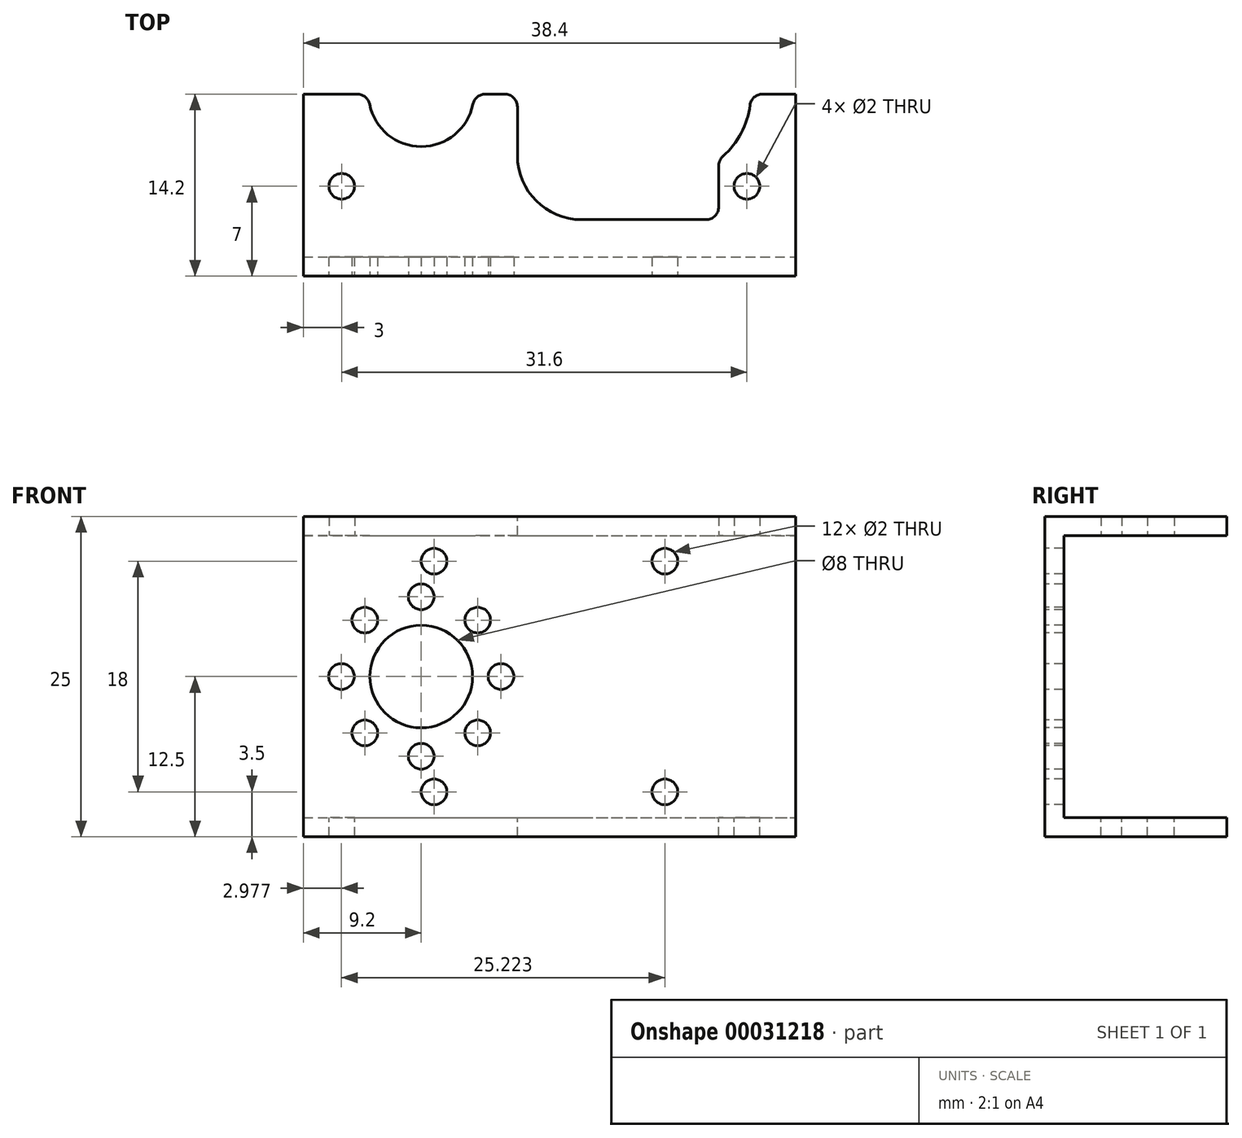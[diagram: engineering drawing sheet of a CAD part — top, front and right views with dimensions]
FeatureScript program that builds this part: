
annotation { "Feature Type Name" : "Feature", "Feature Type Description" : "" }
export const myFeature = defineFeature(function(context is Context, id is Id, definition is map)
    precondition{}
    {
        {
            var Q0;
            Q0=qCreatedBy(makeId("Top.planeOp"),FACE);
            var sketch = newSketch(context, id + "F0", { "sketchPlane" : qUnion([Q0])});
            skLineSegment(sketch, "E0.bottom", {"start": v(19.2, -14.2) * mm, "end": v(-19.2, -14.2) * mm});
            skLineSegment(sketch, "E0.top", {"start": v(19.2, 14.2) * mm, "end": v(-19.2, 14.2) * mm});
            skLineSegment(sketch, "E0.left", {"start": v(19.2, -14.2) * mm, "end": v(19.2, 14.2) * mm});
            skLineSegment(sketch, "E0.right", {"start": v(-19.2, -14.2) * mm, "end": v(-19.2, 14.2) * mm});
            skPoint(sketch, "E0.middle", {"position": v(0, 0) * mm});
            skCircle(sketch, "E1", {"center": v(-10, 0) * mm, "radius": 4.1 * mm});
            skCircle(sketch, "E2", {"center": v(-16.2, 7.2) * mm, "radius": 1 * mm});
            skCircle(sketch, "E3", {"center": v(15.4, 7.2) * mm, "radius": 1 * mm});
            skLineSegment(sketch, "E4.bottom", {"start": v(2.5, 9.8) * mm, "end": v(12.2, 9.8) * mm});
            skLineSegment(sketch, "E4.top", {"start": v(2.5, -9.8) * mm, "end": v(12.2, -9.8) * mm});
            skLineSegment(sketch, "E4.left", {"start": v(-2.5, 4.8) * mm, "end": v(-2.5, -4.8) * mm});
            skLineSegment(sketch, "E4.right", {"start": v(13.2, 8.8) * mm, "end": v(13.2, 5.6) * mm});
            skPoint(sketch, "E4.middle", {"position": v(5.35, 0) * mm});
            skPoint(sketch, "E5.visualSharp", {"position": v(-2.5, 9.8) * mm});
            skArc(sketch, "E5.filletArc", {"start": v(2.5, 9.8) * mm, "mid": v(-1.04, 8.34) * mm, "end": v(-2.5, 4.8) * mm});
            skPoint(sketch, "E6.visualSharp", {"position": v(-2.5, -9.8) * mm});
            skArc(sketch, "E6.filletArc", {"start": v(-2.5, -4.8) * mm, "mid": v(-1.04, -8.34) * mm, "end": v(2.5, -9.8) * mm});
            skPoint(sketch, "E7.visualSharp", {"position": v(13.2, 9.8) * mm});
            skArc(sketch, "E7.filletArc", {"start": v(13.2, 8.8) * mm, "mid": v(12.9, 9.5) * mm, "end": v(12.2, 9.8) * mm});
            skPoint(sketch, "E8.visualSharp", {"position": v(13.2, -9.8) * mm});
            skArc(sketch, "E8.filletArc", {"start": v(12.2, -9.8) * mm, "mid": v(12.9, -9.5) * mm, "end": v(13.2, -8.8) * mm});
            skCircle(sketch, "E9.MirrorC", {"center": v(-16.2, -7.2) * mm, "radius": 1 * mm});
            skCircle(sketch, "E10.MirrorC", {"center": v(15.4, -7.2) * mm, "radius": 1 * mm});
            skArc(sketch, "E11", {"start": v(13.53, -4.84) * mm, "mid": v(15.7, 0) * mm, "end": v(13.53, 4.84) * mm});
            skLineSegment(sketch, "E12.trimOffspring", {"start": v(13.2, -5.6) * mm, "end": v(13.2, -8.8) * mm});
            skPoint(sketch, "E13.visualSharp", {"position": v(13.2, 5.12) * mm});
            skArc(sketch, "E13.filletArc", {"start": v(13.2, 5.6) * mm, "mid": v(13.29, 5.18) * mm, "end": v(13.53, 4.84) * mm});
            skPoint(sketch, "E14.visualSharp", {"position": v(13.2, -5.12) * mm});
            skArc(sketch, "E14.filletArc", {"start": v(13.53, -4.84) * mm, "mid": v(13.29, -5.18) * mm, "end": v(13.2, -5.6) * mm});
            skSolve(sketch);
        }
        {
            var Q0;
            Q0=qSketchRegion(id+"F0",true);
            extrude(context, id + "F1", {"entities" : qUnion([Q0]), "depth" : 1.5 * mm});
        }
        {
            var Q0;
            Q0=makeQuery(id+"F1.opExtrude","CAP_FACE",FACE,{"disambiguationData":[OSD([sQuery(id+"F0.wireOp",EDGE,"E0.bottom"),sQuery(id+"F0.wireOp",EDGE,"E0.top"),sQuery(id+"F0.wireOp",EDGE,"E0.left"),sQuery(id+"F0.wireOp",EDGE,"E0.right"),sQuery(id+"F0.wireOp",EDGE,"E1"),sQuery(id+"F0.wireOp",EDGE,"E2"),sQuery(id+"F0.wireOp",EDGE,"E3"),sQuery(id+"F0.wireOp",EDGE,"E4.bottom"),sQuery(id+"F0.wireOp",EDGE,"E4.top"),sQuery(id+"F0.wireOp",EDGE,"E4.left"),sQuery(id+"F0.wireOp",EDGE,"E4.right"),sQuery(id+"F0.wireOp",EDGE,"E5.filletArc"),sQuery(id+"F0.wireOp",EDGE,"E6.filletArc"),sQuery(id+"F0.wireOp",EDGE,"E7.filletArc"),sQuery(id+"F0.wireOp",EDGE,"E8.filletArc"),sQuery(id+"F0.wireOp",EDGE,"E9.MirrorC"),sQuery(id+"F0.wireOp",EDGE,"E10.MirrorC"),sQuery(id+"F0.wireOp",EDGE,"E11"),sQuery(id+"F0.wireOp",EDGE,"E12.trimOffspring"),sQuery(id+"F0.wireOp",EDGE,"E13.filletArc"),sQuery(id+"F0.wireOp",EDGE,"E14.filletArc")])],"isStart":true});
            var sketch = newSketch(context, id + "F2", { "sketchPlane" : qUnion([Q0])});
            skLineSegment(sketch, "E15.bottom", {"start": v(-19.2, 14.2) * mm, "end": v(19.2, 14.2) * mm});
            skLineSegment(sketch, "E15.top", {"start": v(-19.2, 12.7) * mm, "end": v(19.2, 12.7) * mm});
            skLineSegment(sketch, "E15.left", {"start": v(-19.2, 14.2) * mm, "end": v(-19.2, 12.7) * mm});
            skLineSegment(sketch, "E15.right", {"start": v(19.2, 14.2) * mm, "end": v(19.2, 12.7) * mm});
            skSolve(sketch);
        }
        {
            var Q0;
            Q0=qSketchRegion(id+"F2",true);
            extrude(context, id + "F3", {"entities" : qUnion([Q0]), "operationType" : NewBodyOperationType.ADD, "depth" : (29.3 - 3.8 - 3.5) * mm});
        }
        {
            var Q0;
            Q0=qCreatedBy(makeId("Top.planeOp"),FACE);
            cPlane(context, id + "F4", {"entities" : qUnion([Q0]), "cplaneType" : CPlaneType.OFFSET, "offset" : 11 * mm, "oppositeDirection" : true, "width" : 150 * mm, "height" : 150 * mm});
        }
        {
            var Q0;
            Q0=makeQuery(id+"F1.opExtrude","SWEPT_BODY",BODY,{"disambiguationData":[OSD([sQuery(id+"F0.wireOp",EDGE,"E0.bottom"),sQuery(id+"F0.wireOp",EDGE,"E0.top"),sQuery(id+"F0.wireOp",EDGE,"E0.left"),sQuery(id+"F0.wireOp",EDGE,"E0.right"),sQuery(id+"F0.wireOp",EDGE,"E1"),sQuery(id+"F0.wireOp",EDGE,"E2"),sQuery(id+"F0.wireOp",EDGE,"E3"),sQuery(id+"F0.wireOp",EDGE,"E4.bottom"),sQuery(id+"F0.wireOp",EDGE,"E4.top"),sQuery(id+"F0.wireOp",EDGE,"E4.left"),sQuery(id+"F0.wireOp",EDGE,"E4.right"),sQuery(id+"F0.wireOp",EDGE,"E5.filletArc"),sQuery(id+"F0.wireOp",EDGE,"E6.filletArc"),sQuery(id+"F0.wireOp",EDGE,"E7.filletArc"),sQuery(id+"F0.wireOp",EDGE,"E8.filletArc"),sQuery(id+"F0.wireOp",EDGE,"E9.MirrorC"),sQuery(id+"F0.wireOp",EDGE,"E10.MirrorC"),sQuery(id+"F0.wireOp",EDGE,"E11"),sQuery(id+"F0.wireOp",EDGE,"E12.trimOffspring"),sQuery(id+"F0.wireOp",EDGE,"E13.filletArc"),sQuery(id+"F0.wireOp",EDGE,"E14.filletArc")])]});
            var Q1;
            Q1=qCreatedBy(id+"F4.planeOp",FACE);
            mirror(context, id + "F5", {"operationType" : NewBodyOperationType.ADD, "entities" : qUnion([Q0]), "mirrorPlane" : qUnion([Q1])});
        }
        {
            var Q0;
            Q0=makeQuery(id+"F5.opPattern","COPY",FACE,{"derivedFrom":makeQuery(id+"F1.opExtrude","CAP_FACE",FACE,{"disambiguationData":[OSD([sQuery(id+"F0.wireOp",EDGE,"E0.bottom"),sQuery(id+"F0.wireOp",EDGE,"E0.top"),sQuery(id+"F0.wireOp",EDGE,"E0.left"),sQuery(id+"F0.wireOp",EDGE,"E0.right"),sQuery(id+"F0.wireOp",EDGE,"E1"),sQuery(id+"F0.wireOp",EDGE,"E2"),sQuery(id+"F0.wireOp",EDGE,"E3"),sQuery(id+"F0.wireOp",EDGE,"E4.bottom"),sQuery(id+"F0.wireOp",EDGE,"E4.top"),sQuery(id+"F0.wireOp",EDGE,"E4.left"),sQuery(id+"F0.wireOp",EDGE,"E4.right"),sQuery(id+"F0.wireOp",EDGE,"E5.filletArc"),sQuery(id+"F0.wireOp",EDGE,"E6.filletArc"),sQuery(id+"F0.wireOp",EDGE,"E7.filletArc"),sQuery(id+"F0.wireOp",EDGE,"E8.filletArc"),sQuery(id+"F0.wireOp",EDGE,"E9.MirrorC"),sQuery(id+"F0.wireOp",EDGE,"E10.MirrorC"),sQuery(id+"F0.wireOp",EDGE,"E11"),sQuery(id+"F0.wireOp",EDGE,"E12.trimOffspring"),sQuery(id+"F0.wireOp",EDGE,"E13.filletArc"),sQuery(id+"F0.wireOp",EDGE,"E14.filletArc")])],"isStart":false}),"instanceName":"1"});
            var sketch = newSketch(context, id + "F6", { "sketchPlane" : qUnion([Q0])});
            skLineSegment(sketch, "E16.bottom", {"start": v(-19.2, -14.2) * mm, "end": v(19.2, -14.2) * mm});
            skLineSegment(sketch, "E16.top", {"start": v(-19.2, 0) * mm, "end": v(19.2, 0) * mm});
            skLineSegment(sketch, "E16.left", {"start": v(-19.2, -14.2) * mm, "end": v(-19.2, 0) * mm});
            skLineSegment(sketch, "E16.right", {"start": v(19.2, -14.2) * mm, "end": v(19.2, 0) * mm});
            skSolve(sketch);
        }
        {
            var Q0;
            Q0=qSketchRegion(id+"F6",true);
            extrude(context, id + "F7", {"entities" : qUnion([Q0]), "operationType" : NewBodyOperationType.REMOVE, "endBound" : BoundingType.THROUGH_ALL, "oppositeDirection" : true, "depth" : 25 * mm});
        }
        {
            var Q0;
            {var subQ0=makeQuery(id+"F3.boolean.opBoolean","MERGE",FACE,{"derivedFrom":[makeQuery(id+"F1.opExtrude","SWEPT_FACE",FACE,{"disambiguationData":[OSD([sQuery(id+"F0.wireOp",EDGE,"E0.bottom")])]}),makeQuery(id+"F3.opExtrude","SWEPT_FACE",FACE,{"disambiguationData":[OSD([sQuery(id+"F2.wireOp",EDGE,"E15.bottom")])]})]});Q0=makeQuery(id+"F5.boolean.opBoolean","MERGE",FACE,{"derivedFrom":[subQ0,makeQuery(id+"F5.opPattern","COPY",FACE,{"derivedFrom":subQ0,"instanceName":"1"})]});}
            var sketch = newSketch(context, id + "F8", { "sketchPlane" : qUnion([Q0])});
            skLineSegment(sketch, "E17", {"start": v(-19.2, -11) * mm, "end": v(19.2, -11) * mm, "construction": true});
            skLineSegment(sketch, "E18.bottom", {"start": v(-9, -2) * mm, "end": v(9, -2) * mm, "construction": true});
            skLineSegment(sketch, "E18.top", {"start": v(-9, -20) * mm, "end": v(9, -20) * mm, "construction": true});
            skLineSegment(sketch, "E18.left", {"start": v(-9, -2) * mm, "end": v(-9, -20) * mm, "construction": true});
            skLineSegment(sketch, "E18.right", {"start": v(9, -2) * mm, "end": v(9, -20) * mm, "construction": true});
            skCircle(sketch, "E19", {"center": v(9, -2) * mm, "radius": 1 * mm});
            skCircle(sketch, "E20.MirrorC", {"center": v(-9, -2) * mm, "radius": 1 * mm});
            skCircle(sketch, "E21.MirrorC", {"center": v(-9, -20) * mm, "radius": 1 * mm});
            skCircle(sketch, "E22.MirrorC", {"center": v(9, -20) * mm, "radius": 1 * mm});
            skPoint(sketch, "E23", {"position": v(0, -2) * mm});
            skPoint(sketch, "E24", {"position": v(0, -11) * mm});
            skPoint(sketch, "E25", {"position": v(-9, -11) * mm});
            skLineSegment(sketch, "E26.bottom", {"start": v(-5.6, -6.6) * mm, "end": v(-14.4, -6.6) * mm, "construction": true});
            skLineSegment(sketch, "E26.top", {"start": v(-5.6, -15.4) * mm, "end": v(-14.4, -15.4) * mm, "construction": true});
            skLineSegment(sketch, "E26.left", {"start": v(-5.6, -6.6) * mm, "end": v(-5.6, -15.4) * mm, "construction": true});
            skLineSegment(sketch, "E26.right", {"start": v(-14.4, -6.6) * mm, "end": v(-14.4, -15.4) * mm, "construction": true});
            skPoint(sketch, "E26.middle", {"position": v(-10, -11) * mm});
            skCircle(sketch, "E27", {"center": v(-10, -11) * mm, "radius": 4 * mm});
            skCircle(sketch, "E28", {"center": v(-5.6, -6.6) * mm, "radius": 1 * mm});
            skCircle(sketch, "E29.1.0", {"center": v(-10, -4.78) * mm, "radius": 1 * mm});
            skCircle(sketch, "E29.2.0", {"center": v(-14.4, -6.6) * mm, "radius": 1 * mm});
            skCircle(sketch, "E29.3.0", {"center": v(-16.22, -11) * mm, "radius": 1 * mm});
            skCircle(sketch, "E29.4.0", {"center": v(-14.4, -15.4) * mm, "radius": 1 * mm});
            skCircle(sketch, "E29.5.0", {"center": v(-10, -17.22) * mm, "radius": 1 * mm});
            skCircle(sketch, "E29.6.0", {"center": v(-5.6, -15.4) * mm, "radius": 1 * mm});
            skCircle(sketch, "E29.7.0", {"center": v(-3.78, -11) * mm, "radius": 1 * mm});
            skSolve(sketch);
        }
        {
            var Q0;
            Q0=qSketchRegion(id+"F8",true);
            extrude(context, id + "F9", {"entities" : qUnion([Q0]), "operationType" : NewBodyOperationType.REMOVE, "endBound" : BoundingType.UP_TO_NEXT, "oppositeDirection" : true, "depth" : 25 * mm});
        }
        {
            var Q0;
            Q0=makeQuery(id+"F7.boolean.opBoolean","COPY",EDGE,{"disambiguationData":[OD(0.0)],"derivedFrom":makeQuery(id+"F7.opExtrude","SWEPT_EDGE",EDGE,{"disambiguationData":[OSD([sQuery(id+"F0.wireOp",EDGE,"E0.right"),sQuery(id+"F6.wireOp",EDGE,"E16.top"),sQuery(id+"F6.wireOp",EDGE,"E16.left")])]})});
            var Q1;
            Q1=makeQuery(id+"F7.boolean.opBoolean","COPY",EDGE,{"disambiguationData":[OD(1.0)],"derivedFrom":makeQuery(id+"F7.opExtrude","SWEPT_EDGE",EDGE,{"disambiguationData":[OSD([sQuery(id+"F0.wireOp",EDGE,"E0.right"),sQuery(id+"F6.wireOp",EDGE,"E16.top"),sQuery(id+"F6.wireOp",EDGE,"E16.left")])]})});
            var Q2;
            Q2=makeQuery(id+"F7.boolean.opBoolean","INTERSECT",EDGE,{"disambiguationData":[OD(1.0)],"derivedFrom":[makeQuery(id+"F1.opExtrude","SWEPT_FACE",FACE,{"disambiguationData":[OSD([sQuery(id+"F0.wireOp",EDGE,"E1")])]}),makeQuery(id+"F7.opExtrude","SWEPT_FACE",FACE,{"disambiguationData":[OSD([sQuery(id+"F6.wireOp",EDGE,"E16.top")])]})]});
            var Q3;
            Q3=makeQuery(id+"F7.boolean.opBoolean","INTERSECT",EDGE,{"disambiguationData":[OD(1.0)],"derivedFrom":[makeQuery(id+"F5.opPattern","COPY",FACE,{"derivedFrom":makeQuery(id+"F1.opExtrude","SWEPT_FACE",FACE,{"disambiguationData":[OSD([sQuery(id+"F0.wireOp",EDGE,"E1")])]}),"instanceName":"1"}),makeQuery(id+"F7.opExtrude","SWEPT_FACE",FACE,{"disambiguationData":[OSD([sQuery(id+"F6.wireOp",EDGE,"E16.top")])]})]});
            var Q4;
            Q4=makeQuery(id+"F7.boolean.opBoolean","INTERSECT",EDGE,{"disambiguationData":[OD(0.0)],"derivedFrom":[makeQuery(id+"F5.opPattern","COPY",FACE,{"derivedFrom":makeQuery(id+"F1.opExtrude","SWEPT_FACE",FACE,{"disambiguationData":[OSD([sQuery(id+"F0.wireOp",EDGE,"E1")])]}),"instanceName":"1"}),makeQuery(id+"F7.opExtrude","SWEPT_FACE",FACE,{"disambiguationData":[OSD([sQuery(id+"F6.wireOp",EDGE,"E16.top")])]})]});
            var Q5;
            Q5=makeQuery(id+"F7.boolean.opBoolean","INTERSECT",EDGE,{"derivedFrom":[makeQuery(id+"F5.opPattern","COPY",FACE,{"derivedFrom":makeQuery(id+"F1.opExtrude","SWEPT_FACE",FACE,{"disambiguationData":[OSD([sQuery(id+"F0.wireOp",EDGE,"E4.left")])]}),"instanceName":"1"}),makeQuery(id+"F7.opExtrude","SWEPT_FACE",FACE,{"disambiguationData":[OSD([sQuery(id+"F6.wireOp",EDGE,"E16.top")])]})]});
            var Q6;
            Q6=makeQuery(id+"F7.boolean.opBoolean","INTERSECT",EDGE,{"disambiguationData":[OD(0.0)],"derivedFrom":[makeQuery(id+"F1.opExtrude","SWEPT_FACE",FACE,{"disambiguationData":[OSD([sQuery(id+"F0.wireOp",EDGE,"E1")])]}),makeQuery(id+"F7.opExtrude","SWEPT_FACE",FACE,{"disambiguationData":[OSD([sQuery(id+"F6.wireOp",EDGE,"E16.top")])]})]});
            var Q7;
            Q7=makeQuery(id+"F7.boolean.opBoolean","INTERSECT",EDGE,{"derivedFrom":[makeQuery(id+"F5.opPattern","COPY",FACE,{"derivedFrom":makeQuery(id+"F1.opExtrude","SWEPT_FACE",FACE,{"disambiguationData":[OSD([sQuery(id+"F0.wireOp",EDGE,"E11")])]}),"instanceName":"1"}),makeQuery(id+"F7.opExtrude","SWEPT_FACE",FACE,{"disambiguationData":[OSD([sQuery(id+"F6.wireOp",EDGE,"E16.top")])]})]});
            var Q8;
            Q8=makeQuery(id+"F7.boolean.opBoolean","INTERSECT",EDGE,{"derivedFrom":[makeQuery(id+"F1.opExtrude","SWEPT_FACE",FACE,{"disambiguationData":[OSD([sQuery(id+"F0.wireOp",EDGE,"E11")])]}),makeQuery(id+"F7.opExtrude","SWEPT_FACE",FACE,{"disambiguationData":[OSD([sQuery(id+"F6.wireOp",EDGE,"E16.top")])]})]});
            var Q9;
            Q9=makeQuery(id+"F7.boolean.opBoolean","COPY",EDGE,{"disambiguationData":[OD(0.0)],"derivedFrom":makeQuery(id+"F7.opExtrude","SWEPT_EDGE",EDGE,{"disambiguationData":[OSD([sQuery(id+"F0.wireOp",EDGE,"E0.left"),sQuery(id+"F6.wireOp",EDGE,"E16.top"),sQuery(id+"F6.wireOp",EDGE,"E16.right")])]})});
            var Q10;
            Q10=makeQuery(id+"F7.boolean.opBoolean","INTERSECT",EDGE,{"derivedFrom":[makeQuery(id+"F1.opExtrude","SWEPT_FACE",FACE,{"disambiguationData":[OSD([sQuery(id+"F0.wireOp",EDGE,"E4.left")])]}),makeQuery(id+"F7.opExtrude","SWEPT_FACE",FACE,{"disambiguationData":[OSD([sQuery(id+"F6.wireOp",EDGE,"E16.top")])]})]});
            var Q11;
            Q11=makeQuery(id+"F7.boolean.opBoolean","COPY",EDGE,{"disambiguationData":[OD(1.0)],"derivedFrom":makeQuery(id+"F7.opExtrude","SWEPT_EDGE",EDGE,{"disambiguationData":[OSD([sQuery(id+"F0.wireOp",EDGE,"E0.left"),sQuery(id+"F6.wireOp",EDGE,"E16.top"),sQuery(id+"F6.wireOp",EDGE,"E16.right")])]})});
            fillet(context, id + "F10", {"entities" : qUnion([Q0, Q1, Q2, Q3, Q4, Q5, Q6, Q7, Q8, Q9, Q10, Q11]), "radius" : 1 * mm, "tangentPropagation" : true, "allowEdgeOverflow" : false});
        }
    });
